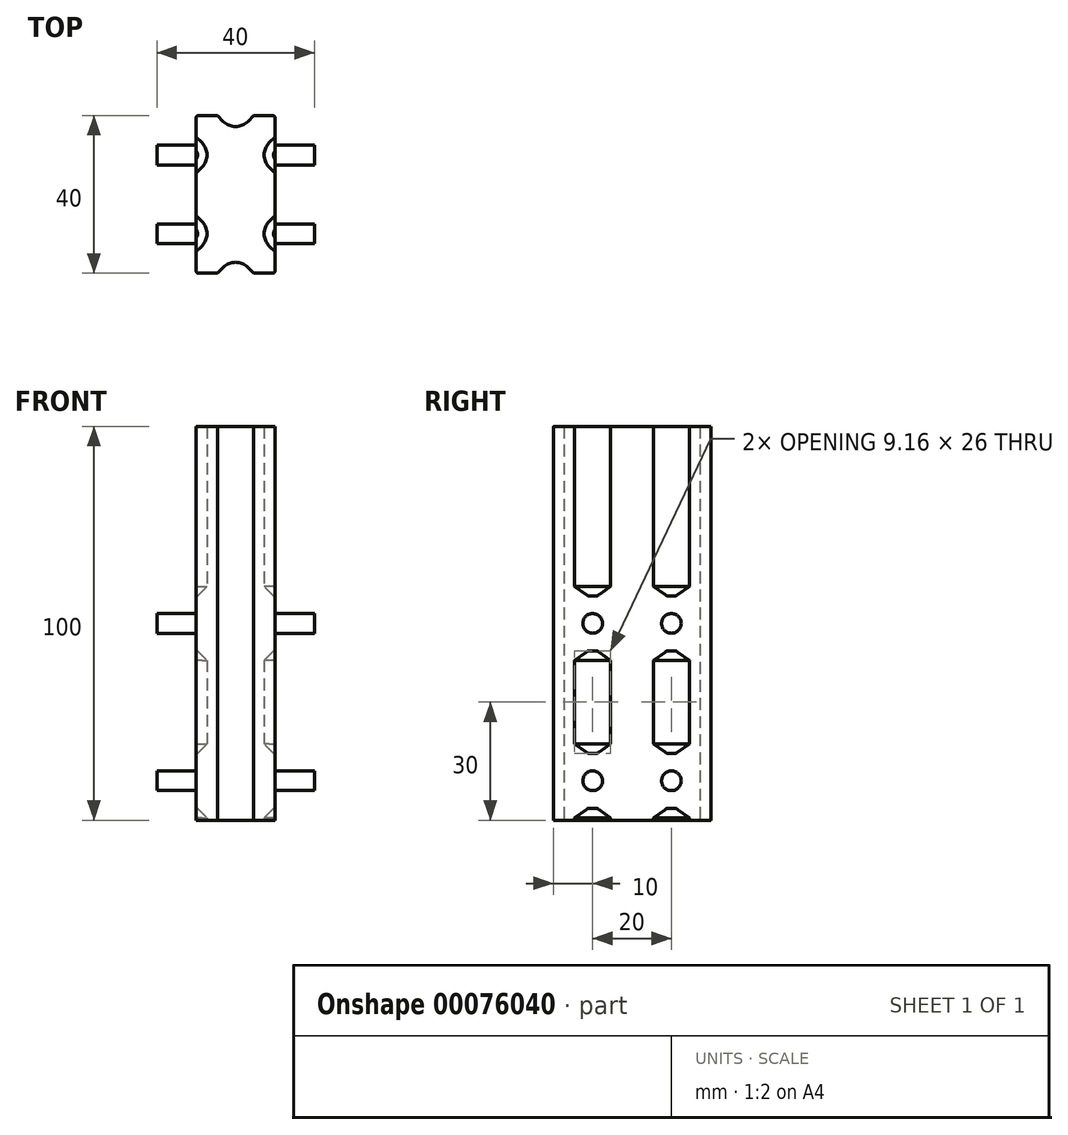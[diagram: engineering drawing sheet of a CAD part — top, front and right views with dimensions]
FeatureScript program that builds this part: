
annotation { "Feature Type Name" : "Feature", "Feature Type Description" : "" }
export const myFeature = defineFeature(function(context is Context, id is Id, definition is map)
    precondition{}
    {
        {
            var Q0;
            Q0=qCreatedBy(makeId("Top.planeOp"),FACE);
            var sketch = newSketch(context, id + "F0", { "sketchPlane" : qUnion([Q0])});
            skLineSegment(sketch, "E0.0.56", {"start": v(-10, 0) * mm, "end": v(-10, 5.42) * mm});
            skLineSegment(sketch, "E0.0.57", {"start": v(-10, 5.42) * mm, "end": v(-8.54, 6.88) * mm});
            skLineSegment(sketch, "E0.0.58", {"start": v(-8.54, 6.87) * mm, "end": v(-8.2, 6.87) * mm});
            skLineSegment(sketch, "E0.0.69", {"start": v(-8.2, 13.12) * mm, "end": v(-8.54, 13.12) * mm});
            skLineSegment(sketch, "E0.0.70", {"start": v(-8.54, 13.12) * mm, "end": v(-10, 14.58) * mm});
            skLineSegment(sketch, "E0.0.71", {"start": v(-10, 14.58) * mm, "end": v(-10, 19.5) * mm});
            skArc(sketch, "E0.0.72", {"start": v(-10, 19.5) * mm, "mid": v(-9.85, 19.85) * mm, "end": v(-9.5, 20) * mm});
            skLineSegment(sketch, "E0.0.73", {"start": v(-9.5, 20) * mm, "end": v(-4.58, 20) * mm});
            skLineSegment(sketch, "E0.0.74", {"start": v(-4.58, 20) * mm, "end": v(-3.12, 18.55) * mm});
            skLineSegment(sketch, "E0.0.75", {"start": v(-3.12, 18.55) * mm, "end": v(-3.12, 18.2) * mm});
            skLineSegment(sketch, "E1", {"start": v(-3.12, 18.2) * mm, "end": v(-3.12, 16.2) * mm});
            skLineSegment(sketch, "E2", {"start": v(0, 16.2) * mm, "end": v(-3.12, 16.2) * mm});
            skLineSegment(sketch, "E3", {"start": v(-6.2, 6.88) * mm, "end": v(-6.2, 13.13) * mm});
            skLineSegment(sketch, "E4.trimOffspring", {"start": v(-6.2, 13.12) * mm, "end": v(-8.2, 13.12) * mm});
            skLineSegment(sketch, "E5", {"start": v(-8.2, 6.87) * mm, "end": v(-6.2, 6.87) * mm});
            skLineSegment(sketch, "E6.MirrorCS", {"start": v(8.2, 13.12) * mm, "end": v(8.54, 13.12) * mm});
            skLineSegment(sketch, "E7.MirrorCS", {"start": v(8.54, 6.87) * mm, "end": v(8.2, 6.87) * mm});
            skLineSegment(sketch, "E8.MirrorCS", {"start": v(3.12, 18.55) * mm, "end": v(3.12, 18.2) * mm});
            skLineSegment(sketch, "E9.MirrorCS", {"start": v(6.2, 6.88) * mm, "end": v(6.2, 13.13) * mm});
            skLineSegment(sketch, "E10.MirrorCS", {"start": v(4.58, 20) * mm, "end": v(3.12, 18.55) * mm});
            skLineSegment(sketch, "E11.MirrorCS", {"start": v(0, 16.2) * mm, "end": v(3.12, 16.2) * mm});
            skLineSegment(sketch, "E12.MirrorCS", {"start": v(10, 0) * mm, "end": v(10, 5.42) * mm});
            skLineSegment(sketch, "E13.MirrorCS", {"start": v(8.54, 13.12) * mm, "end": v(10, 14.58) * mm});
            skLineSegment(sketch, "E14.MirrorCS", {"start": v(9.5, 20) * mm, "end": v(4.58, 20) * mm});
            skLineSegment(sketch, "E15.MirrorCS", {"start": v(6.2, 13.12) * mm, "end": v(8.2, 13.12) * mm});
            skLineSegment(sketch, "E16.MirrorCS", {"start": v(10, 14.58) * mm, "end": v(10, 19.5) * mm});
            skLineSegment(sketch, "E17.MirrorCS", {"start": v(10, 5.42) * mm, "end": v(8.54, 6.88) * mm});
            skArc(sketch, "E18.MirrorCS", {"start": v(10, 19.5) * mm, "mid": v(9.85, 19.85) * mm, "end": v(9.5, 20) * mm});
            skLineSegment(sketch, "E19.MirrorCS", {"start": v(3.12, 18.2) * mm, "end": v(3.12, 16.2) * mm});
            skLineSegment(sketch, "E20.MirrorCS", {"start": v(8.2, 6.87) * mm, "end": v(6.2, 6.87) * mm});
            skLineSegment(sketch, "E21.MirrorCS", {"start": v(3.12, -18.55) * mm, "end": v(3.12, -18.2) * mm});
            skLineSegment(sketch, "E22.MirrorCS", {"start": v(8.2, -13.12) * mm, "end": v(8.54, -13.12) * mm});
            skLineSegment(sketch, "E23.MirrorCS", {"start": v(8.54, -6.87) * mm, "end": v(8.2, -6.87) * mm});
            skLineSegment(sketch, "E24.MirrorCS", {"start": v(-8.2, -13.12) * mm, "end": v(-8.54, -13.12) * mm});
            skLineSegment(sketch, "E25.MirrorCS", {"start": v(-3.12, -18.55) * mm, "end": v(-3.12, -18.2) * mm});
            skLineSegment(sketch, "E26.MirrorCS", {"start": v(-8.54, -6.87) * mm, "end": v(-8.2, -6.87) * mm});
            skLineSegment(sketch, "E27.MirrorCS", {"start": v(-3.12, -18.2) * mm, "end": v(-3.12, -16.2) * mm});
            skLineSegment(sketch, "E28.MirrorCS", {"start": v(0, -16.2) * mm, "end": v(-3.12, -16.2) * mm});
            skLineSegment(sketch, "E29.MirrorCS", {"start": v(-9.5, -20) * mm, "end": v(-4.58, -20) * mm});
            skLineSegment(sketch, "E30.MirrorCS", {"start": v(0, -16.2) * mm, "end": v(3.12, -16.2) * mm});
            skLineSegment(sketch, "E31.MirrorCS", {"start": v(10, 0) * mm, "end": v(10, -5.42) * mm});
            skLineSegment(sketch, "E32.MirrorCS", {"start": v(3.12, -18.2) * mm, "end": v(3.12, -16.2) * mm});
            skLineSegment(sketch, "E33.MirrorCS", {"start": v(-6.2, -13.12) * mm, "end": v(-8.2, -13.12) * mm});
            skLineSegment(sketch, "E34.MirrorCS", {"start": v(10, -14.58) * mm, "end": v(10, -19.5) * mm});
            skLineSegment(sketch, "E35.MirrorCS", {"start": v(-6.2, -6.88) * mm, "end": v(-6.2, -13.13) * mm});
            skLineSegment(sketch, "E36.MirrorCS", {"start": v(6.2, -6.88) * mm, "end": v(6.2, -13.13) * mm});
            skLineSegment(sketch, "E37.MirrorCS", {"start": v(4.58, -20) * mm, "end": v(3.12, -18.55) * mm});
            skLineSegment(sketch, "E38.MirrorCS", {"start": v(-10, -5.42) * mm, "end": v(-8.54, -6.88) * mm});
            skLineSegment(sketch, "E39.MirrorCS", {"start": v(-10, -14.58) * mm, "end": v(-10, -19.5) * mm});
            skLineSegment(sketch, "E40.MirrorCS", {"start": v(-8.2, -6.87) * mm, "end": v(-6.2, -6.87) * mm});
            skLineSegment(sketch, "E41.MirrorCS", {"start": v(10, -5.42) * mm, "end": v(8.54, -6.88) * mm});
            skLineSegment(sketch, "E42.MirrorCS", {"start": v(-4.58, -20) * mm, "end": v(-3.12, -18.55) * mm});
            skLineSegment(sketch, "E43.MirrorCS", {"start": v(9.5, -20) * mm, "end": v(4.58, -20) * mm});
            skLineSegment(sketch, "E44.MirrorCS", {"start": v(-10, 0) * mm, "end": v(-10, -5.42) * mm});
            skLineSegment(sketch, "E45.MirrorCS", {"start": v(-8.54, -13.12) * mm, "end": v(-10, -14.58) * mm});
            skArc(sketch, "E46.MirrorCS", {"start": v(10, -19.5) * mm, "mid": v(9.85, -19.85) * mm, "end": v(9.5, -20) * mm});
            skLineSegment(sketch, "E47.MirrorCS", {"start": v(8.54, -13.12) * mm, "end": v(10, -14.58) * mm});
            skLineSegment(sketch, "E48.MirrorCS", {"start": v(8.2, -6.87) * mm, "end": v(6.2, -6.87) * mm});
            skArc(sketch, "E49.MirrorCS", {"start": v(-10, -19.5) * mm, "mid": v(-9.85, -19.85) * mm, "end": v(-9.5, -20) * mm});
            skLineSegment(sketch, "E50.MirrorCS", {"start": v(6.2, -13.12) * mm, "end": v(8.2, -13.12) * mm});
            skArc(sketch, "E51", {"start": v(-3.12, 18.55) * mm, "mid": v(0, 17.25) * mm, "end": v(3.12, 18.55) * mm});
            skArc(sketch, "E52", {"start": v(-8.54, 6.88) * mm, "mid": v(-7.25, 10) * mm, "end": v(-8.54, 13.12) * mm});
            skArc(sketch, "E53", {"start": v(8.54, 13.12) * mm, "mid": v(7.25, 10) * mm, "end": v(8.54, 6.87) * mm});
            skArc(sketch, "E54", {"start": v(-8.54, -13.12) * mm, "mid": v(-7.25, -10) * mm, "end": v(-8.54, -6.87) * mm});
            skArc(sketch, "E55", {"start": v(8.54, -6.87) * mm, "mid": v(7.25, -10) * mm, "end": v(8.54, -13.12) * mm});
            skArc(sketch, "E56", {"start": v(3.12, -18.55) * mm, "mid": v(0, -17.25) * mm, "end": v(-3.12, -18.55) * mm});
            skSolve(sketch);
        }
        {
            var Q0;
            Q0=makeQuery(id+"F0.imprint","IMPRINT",FACE,{"disambiguationData":[TD([[makeQuery(id+"F0.imprint","IMPRINT",EDGE,{"derivedFrom":sQuery(id+"F0.wireOp",EDGE,"E0.0.56")}),-1.0]])]});
            var Q1;
            Q1=makeQuery(id+"F0.imprint","IMPRINT",FACE,{"disambiguationData":[TD([[makeQuery(id+"F0.imprint","IMPRINT",EDGE,{"derivedFrom":sQuery(id+"F0.wireOp",EDGE,"E6.MirrorCS")}),-1.0]])]});
            var Q2;
            Q2=makeQuery(id+"F0.imprint","IMPRINT",FACE,{"disambiguationData":[TD([[makeQuery(id+"F0.imprint","IMPRINT",EDGE,{"derivedFrom":sQuery(id+"F0.wireOp",EDGE,"E22.MirrorCS")}),1.0]])]});
            var Q3;
            Q3=makeQuery(id+"F0.imprint","IMPRINT",FACE,{"disambiguationData":[TD([[makeQuery(id+"F0.imprint","IMPRINT",EDGE,{"derivedFrom":sQuery(id+"F0.wireOp",EDGE,"E21.MirrorCS")}),1.0]])]});
            var Q4;
            Q4=makeQuery(id+"F0.imprint","IMPRINT",FACE,{"disambiguationData":[TD([[makeQuery(id+"F0.imprint","IMPRINT",EDGE,{"derivedFrom":sQuery(id+"F0.wireOp",EDGE,"E24.MirrorCS")}),-1.0]])]});
            var Q5;
            Q5=makeQuery(id+"F0.imprint","IMPRINT",FACE,{"disambiguationData":[TD([[makeQuery(id+"F0.imprint","IMPRINT",EDGE,{"derivedFrom":sQuery(id+"F0.wireOp",EDGE,"E0.0.58")}),1.0]])]});
            var Q6;
            Q6=makeQuery(id+"F0.imprint","IMPRINT",FACE,{"disambiguationData":[TD([[makeQuery(id+"F0.imprint","IMPRINT",EDGE,{"derivedFrom":sQuery(id+"F0.wireOp",EDGE,"E0.0.75")}),1.0]])]});
            extrude(context, id + "F1", {"entities" : qUnion([Q0, Q1, Q2, Q3, Q4, Q5, Q6]), "depth" : 100 * mm});
        }
        {
            var Q0;
            Q0=qCreatedBy(makeId("Right.planeOp"),FACE);
            var sketch = newSketch(context, id + "F2", { "sketchPlane" : qUnion([Q0])});
            skLineSegment(sketch, "E57.0", {"start": v(-5.42, 0) * mm, "end": v(5.42, 0) * mm, "construction": true});
            skLineSegment(sketch, "E58.1", {"start": v(20, 100) * mm, "end": v(20, 0) * mm});
            skLineSegment(sketch, "E59.0", {"start": v(-20, 100) * mm, "end": v(-20, 0) * mm});
            skLineSegment(sketch, "E60.bottom", {"start": v(20, 0) * mm, "end": v(10, 0) * mm, "construction": true});
            skLineSegment(sketch, "E60.top", {"start": v(20, 10) * mm, "end": v(10, 10) * mm, "construction": true});
            skLineSegment(sketch, "E60.left", {"start": v(20, 0) * mm, "end": v(20, 10) * mm, "construction": true});
            skLineSegment(sketch, "E60.right", {"start": v(10, 0) * mm, "end": v(10, 10) * mm, "construction": true});
            skLineSegment(sketch, "E61.bottom", {"start": v(-20, 0) * mm, "end": v(-10, 0) * mm, "construction": true});
            skLineSegment(sketch, "E61.top", {"start": v(-20, 10) * mm, "end": v(-10, 10) * mm, "construction": true});
            skLineSegment(sketch, "E61.left", {"start": v(-20, 0) * mm, "end": v(-20, 10) * mm, "construction": true});
            skLineSegment(sketch, "E61.right", {"start": v(-10, 0) * mm, "end": v(-10, 10) * mm, "construction": true});
            skLineSegment(sketch, "E62.bottom", {"start": v(-10, 10) * mm, "end": v(10, 10) * mm, "construction": true});
            skLineSegment(sketch, "E62.top", {"start": v(-10, 50) * mm, "end": v(10, 50) * mm, "construction": true});
            skLineSegment(sketch, "E62.left", {"start": v(-10, 10) * mm, "end": v(-10, 50) * mm, "construction": true});
            skLineSegment(sketch, "E62.right", {"start": v(10, 10) * mm, "end": v(10, 50) * mm, "construction": true});
            skCircle(sketch, "E63", {"center": v(10, 50) * mm, "radius": 2.5 * mm});
            skCircle(sketch, "E64", {"center": v(-10, 50) * mm, "radius": 2.5 * mm});
            skCircle(sketch, "E65", {"center": v(-10, 10) * mm, "radius": 2.5 * mm});
            skCircle(sketch, "E66", {"center": v(10, 10) * mm, "radius": 2.5 * mm});
            skLineSegment(sketch, "E67.bottom", {"start": v(3, 43) * mm, "end": v(17, 43) * mm});
            skLineSegment(sketch, "E67.top", {"start": v(3, 57) * mm, "end": v(17, 57) * mm});
            skLineSegment(sketch, "E67.left", {"start": v(3, 43) * mm, "end": v(3, 57) * mm});
            skLineSegment(sketch, "E67.right", {"start": v(17, 43) * mm, "end": v(17, 57) * mm});
            skLineSegment(sketch, "E68.bottom", {"start": v(-3, 57) * mm, "end": v(-17, 57) * mm});
            skLineSegment(sketch, "E68.top", {"start": v(-3, 43) * mm, "end": v(-17, 43) * mm});
            skLineSegment(sketch, "E68.left", {"start": v(-3, 57) * mm, "end": v(-3, 43) * mm});
            skLineSegment(sketch, "E68.right", {"start": v(-17, 57) * mm, "end": v(-17, 43) * mm});
            skLineSegment(sketch, "E69.bottom", {"start": v(17, 17) * mm, "end": v(3, 17) * mm});
            skLineSegment(sketch, "E69.top", {"start": v(17, 3) * mm, "end": v(3, 3) * mm});
            skLineSegment(sketch, "E69.left", {"start": v(17, 17) * mm, "end": v(17, 3) * mm});
            skLineSegment(sketch, "E69.right", {"start": v(3, 17) * mm, "end": v(3, 3) * mm});
            skLineSegment(sketch, "E70.bottom", {"start": v(-3, 17) * mm, "end": v(-17, 17) * mm});
            skLineSegment(sketch, "E70.top", {"start": v(-3, 3) * mm, "end": v(-17, 3) * mm});
            skLineSegment(sketch, "E70.left", {"start": v(-3, 17) * mm, "end": v(-3, 3) * mm});
            skLineSegment(sketch, "E70.right", {"start": v(-17, 17) * mm, "end": v(-17, 3) * mm});
            skLineSegment(sketch, "E71.bottom", {"start": v(17, 17) * mm, "end": v(20, 17) * mm});
            skLineSegment(sketch, "E71.top", {"start": v(17, 3) * mm, "end": v(20, 3) * mm});
            skLineSegment(sketch, "E71.right", {"start": v(20, 17) * mm, "end": v(20, 3) * mm});
            skLineSegment(sketch, "E72.bottom", {"start": v(-17, 17) * mm, "end": v(-20, 17) * mm});
            skLineSegment(sketch, "E72.top", {"start": v(-17, 3) * mm, "end": v(-20, 3) * mm});
            skLineSegment(sketch, "E72.right", {"start": v(-20, 17) * mm, "end": v(-20, 3) * mm});
            skSolve(sketch);
        }
        {
            var Q0;
            Q0=makeQuery(id+"F2.imprint","IMPRINT",FACE,{"disambiguationData":[TD([[makeQuery(id+"F2.imprint","IMPRINT",EDGE,{"derivedFrom":sQuery(id+"F2.wireOp",EDGE,"E63")}),-1.0]])]});
            var Q1;
            Q1=makeQuery(id+"F2.imprint","IMPRINT",FACE,{"disambiguationData":[TD([[makeQuery(id+"F2.imprint","IMPRINT",EDGE,{"derivedFrom":sQuery(id+"F2.wireOp",EDGE,"E64")}),-1.0]])]});
            var Q2;
            Q2=makeQuery(id+"F2.imprint","IMPRINT",FACE,{"disambiguationData":[TD([[makeQuery(id+"F2.imprint","IMPRINT",EDGE,{"derivedFrom":sQuery(id+"F2.wireOp",EDGE,"E65")}),-1.0]])]});
            var Q3;
            Q3=makeQuery(id+"F2.imprint","IMPRINT",FACE,{"disambiguationData":[TD([[makeQuery(id+"F2.imprint","IMPRINT",EDGE,{"derivedFrom":sQuery(id+"F2.wireOp",EDGE,"E66")}),-1.0]])]});
            extrude(context, id + "F3", {"entities" : qUnion([Q0, Q1, Q2, Q3]), "operationType" : NewBodyOperationType.ADD, "endBound" : BoundingType.SYMMETRIC, "depth" : 20 * mm});
        }
        {
            var Q0;
            Q0=makeQuery(id+"F2.imprint","IMPRINT",FACE,{"disambiguationData":[TD([[makeQuery(id+"F2.imprint","IMPRINT",EDGE,{"derivedFrom":sQuery(id+"F2.wireOp",EDGE,"E66")}),1.0]])]});
            var Q1;
            Q1=makeQuery(id+"F2.imprint","IMPRINT",FACE,{"disambiguationData":[TD([[makeQuery(id+"F2.imprint","IMPRINT",EDGE,{"derivedFrom":sQuery(id+"F2.wireOp",EDGE,"E63")}),1.0]])]});
            var Q2;
            Q2=makeQuery(id+"F2.imprint","IMPRINT",FACE,{"disambiguationData":[TD([[makeQuery(id+"F2.imprint","IMPRINT",EDGE,{"derivedFrom":sQuery(id+"F2.wireOp",EDGE,"E65")}),1.0]])]});
            var Q3;
            Q3=makeQuery(id+"F2.imprint","IMPRINT",FACE,{"disambiguationData":[TD([[makeQuery(id+"F2.imprint","IMPRINT",EDGE,{"derivedFrom":sQuery(id+"F2.wireOp",EDGE,"E64")}),1.0]])]});
            extrude(context, id + "F4", {"entities" : qUnion([Q0, Q1, Q2, Q3]), "operationType" : NewBodyOperationType.ADD, "endBound" : BoundingType.SYMMETRIC, "depth" : 40 * mm});
        }
        {
            var Q0;
            Q0=makeQuery(id+"F3.boolean.opBoolean","INTERSECT",EDGE,{"derivedFrom":[makeQuery(id+"F1.opExtrude","SWEPT_FACE",FACE,{"disambiguationData":[OSD([sQuery(id+"F0.wireOp",EDGE,"E52")])]}),makeQuery(id+"F3.opExtrude","SWEPT_FACE",FACE,{"disambiguationData":[OSD([sQuery(id+"F2.wireOp",EDGE,"E67.bottom")])]})]});
            var Q1;
            Q1=makeQuery(id+"F3.boolean.opBoolean","INTERSECT",EDGE,{"derivedFrom":[makeQuery(id+"F1.opExtrude","SWEPT_FACE",FACE,{"disambiguationData":[OSD([sQuery(id+"F0.wireOp",EDGE,"E52")])]}),makeQuery(id+"F3.opExtrude","SWEPT_FACE",FACE,{"disambiguationData":[OSD([sQuery(id+"F2.wireOp",EDGE,"E69.bottom")])]})]});
            var Q2;
            Q2=makeQuery(id+"F3.boolean.opBoolean","INTERSECT",EDGE,{"derivedFrom":[makeQuery(id+"F1.opExtrude","SWEPT_FACE",FACE,{"disambiguationData":[OSD([sQuery(id+"F0.wireOp",EDGE,"E52")])]}),makeQuery(id+"F3.opExtrude","SWEPT_FACE",FACE,{"disambiguationData":[OSD([sQuery(id+"F2.wireOp",EDGE,"E67.top")])]})]});
            var Q3;
            Q3=makeQuery(id+"F3.boolean.opBoolean","INTERSECT",EDGE,{"derivedFrom":[makeQuery(id+"F1.opExtrude","SWEPT_FACE",FACE,{"disambiguationData":[OSD([sQuery(id+"F0.wireOp",EDGE,"E54")])]}),makeQuery(id+"F3.opExtrude","SWEPT_FACE",FACE,{"disambiguationData":[OSD([sQuery(id+"F2.wireOp",EDGE,"E68.bottom")])]})]});
            var Q4;
            Q4=makeQuery(id+"F3.boolean.opBoolean","INTERSECT",EDGE,{"derivedFrom":[makeQuery(id+"F1.opExtrude","SWEPT_FACE",FACE,{"disambiguationData":[OSD([sQuery(id+"F0.wireOp",EDGE,"E54")])]}),makeQuery(id+"F3.opExtrude","SWEPT_FACE",FACE,{"disambiguationData":[OSD([sQuery(id+"F2.wireOp",EDGE,"E70.bottom")])]})]});
            var Q5;
            Q5=makeQuery(id+"F3.boolean.opBoolean","INTERSECT",EDGE,{"derivedFrom":[makeQuery(id+"F1.opExtrude","SWEPT_FACE",FACE,{"disambiguationData":[OSD([sQuery(id+"F0.wireOp",EDGE,"E54")])]}),makeQuery(id+"F3.opExtrude","SWEPT_FACE",FACE,{"disambiguationData":[OSD([sQuery(id+"F2.wireOp",EDGE,"E68.top")])]})]});
            var Q6;
            Q6=makeQuery(id+"F3.boolean.opBoolean","INTERSECT",EDGE,{"derivedFrom":[makeQuery(id+"F1.opExtrude","SWEPT_FACE",FACE,{"disambiguationData":[OSD([sQuery(id+"F0.wireOp",EDGE,"E54")])]}),makeQuery(id+"F3.opExtrude","SWEPT_FACE",FACE,{"disambiguationData":[OSD([sQuery(id+"F2.wireOp",EDGE,"E70.top")])]})]});
            var Q7;
            Q7=makeQuery(id+"F3.boolean.opBoolean","INTERSECT",EDGE,{"derivedFrom":[makeQuery(id+"F1.opExtrude","SWEPT_FACE",FACE,{"disambiguationData":[OSD([sQuery(id+"F0.wireOp",EDGE,"E52")])]}),makeQuery(id+"F3.opExtrude","SWEPT_FACE",FACE,{"disambiguationData":[OSD([sQuery(id+"F2.wireOp",EDGE,"E69.top")])]})]});
            var Q8;
            Q8=makeQuery(id+"F3.boolean.opBoolean","INTERSECT",EDGE,{"derivedFrom":[makeQuery(id+"F1.opExtrude","SWEPT_FACE",FACE,{"disambiguationData":[OSD([sQuery(id+"F0.wireOp",EDGE,"E55")])]}),makeQuery(id+"F3.opExtrude","SWEPT_FACE",FACE,{"disambiguationData":[OSD([sQuery(id+"F2.wireOp",EDGE,"E68.bottom")])]})]});
            var Q9;
            Q9=makeQuery(id+"F3.boolean.opBoolean","INTERSECT",EDGE,{"derivedFrom":[makeQuery(id+"F1.opExtrude","SWEPT_FACE",FACE,{"disambiguationData":[OSD([sQuery(id+"F0.wireOp",EDGE,"E55")])]}),makeQuery(id+"F3.opExtrude","SWEPT_FACE",FACE,{"disambiguationData":[OSD([sQuery(id+"F2.wireOp",EDGE,"E70.bottom")])]})]});
            var Q10;
            Q10=makeQuery(id+"F3.boolean.opBoolean","INTERSECT",EDGE,{"derivedFrom":[makeQuery(id+"F1.opExtrude","SWEPT_FACE",FACE,{"disambiguationData":[OSD([sQuery(id+"F0.wireOp",EDGE,"E53")])]}),makeQuery(id+"F3.opExtrude","SWEPT_FACE",FACE,{"disambiguationData":[OSD([sQuery(id+"F2.wireOp",EDGE,"E69.bottom")])]})]});
            var Q11;
            Q11=makeQuery(id+"F3.boolean.opBoolean","INTERSECT",EDGE,{"derivedFrom":[makeQuery(id+"F1.opExtrude","SWEPT_FACE",FACE,{"disambiguationData":[OSD([sQuery(id+"F0.wireOp",EDGE,"E53")])]}),makeQuery(id+"F3.opExtrude","SWEPT_FACE",FACE,{"disambiguationData":[OSD([sQuery(id+"F2.wireOp",EDGE,"E67.top")])]})]});
            var Q12;
            Q12=makeQuery(id+"F3.boolean.opBoolean","INTERSECT",EDGE,{"derivedFrom":[makeQuery(id+"F1.opExtrude","SWEPT_FACE",FACE,{"disambiguationData":[OSD([sQuery(id+"F0.wireOp",EDGE,"E53")])]}),makeQuery(id+"F3.opExtrude","SWEPT_FACE",FACE,{"disambiguationData":[OSD([sQuery(id+"F2.wireOp",EDGE,"E67.bottom")])]})]});
            var Q13;
            Q13=makeQuery(id+"F3.boolean.opBoolean","INTERSECT",EDGE,{"derivedFrom":[makeQuery(id+"F1.opExtrude","SWEPT_FACE",FACE,{"disambiguationData":[OSD([sQuery(id+"F0.wireOp",EDGE,"E55")])]}),makeQuery(id+"F3.opExtrude","SWEPT_FACE",FACE,{"disambiguationData":[OSD([sQuery(id+"F2.wireOp",EDGE,"E68.top")])]})]});
            var Q14;
            Q14=makeQuery(id+"F3.boolean.opBoolean","INTERSECT",EDGE,{"derivedFrom":[makeQuery(id+"F1.opExtrude","SWEPT_FACE",FACE,{"disambiguationData":[OSD([sQuery(id+"F0.wireOp",EDGE,"E55")])]}),makeQuery(id+"F3.opExtrude","SWEPT_FACE",FACE,{"disambiguationData":[OSD([sQuery(id+"F2.wireOp",EDGE,"E70.top")])]})]});
            var Q15;
            Q15=makeQuery(id+"F3.boolean.opBoolean","INTERSECT",EDGE,{"derivedFrom":[makeQuery(id+"F1.opExtrude","SWEPT_FACE",FACE,{"disambiguationData":[OSD([sQuery(id+"F0.wireOp",EDGE,"E53")])]}),makeQuery(id+"F3.opExtrude","SWEPT_FACE",FACE,{"disambiguationData":[OSD([sQuery(id+"F2.wireOp",EDGE,"E69.top")])]})]});
            var Q16;
            Q16=makeQuery(id+"F3.boolean.opBoolean","INTERSECT",EDGE,{"derivedFrom":[makeQuery(id+"F1.opExtrude","SWEPT_FACE",FACE,{"disambiguationData":[OSD([sQuery(id+"F0.wireOp",EDGE,"E56")])]}),makeQuery(id+"F3.opExtrude","SWEPT_FACE",FACE,{"disambiguationData":[OSD([sQuery(id+"F2.wireOp",EDGE,"E70.bottom"),sQuery(id+"F2.wireOp",EDGE,"E72.bottom")])]})]});
            var Q17;
            Q17=makeQuery(id+"F3.boolean.opBoolean","INTERSECT",EDGE,{"derivedFrom":[makeQuery(id+"F1.opExtrude","SWEPT_FACE",FACE,{"disambiguationData":[OSD([sQuery(id+"F0.wireOp",EDGE,"E56")])]}),makeQuery(id+"F3.opExtrude","SWEPT_FACE",FACE,{"disambiguationData":[OSD([sQuery(id+"F2.wireOp",EDGE,"E70.top"),sQuery(id+"F2.wireOp",EDGE,"E72.top")])]})]});
            chamfer(context, id + "F5", {"entities" : qUnion([Q0, Q1, Q2, Q3, Q4, Q5, Q6, Q7, Q8, Q9, Q10, Q11, Q12, Q13, Q14, Q15, Q16, Q17]), "width" : 2.4 * mm, "tangentPropagation" : true});
        }
    });
